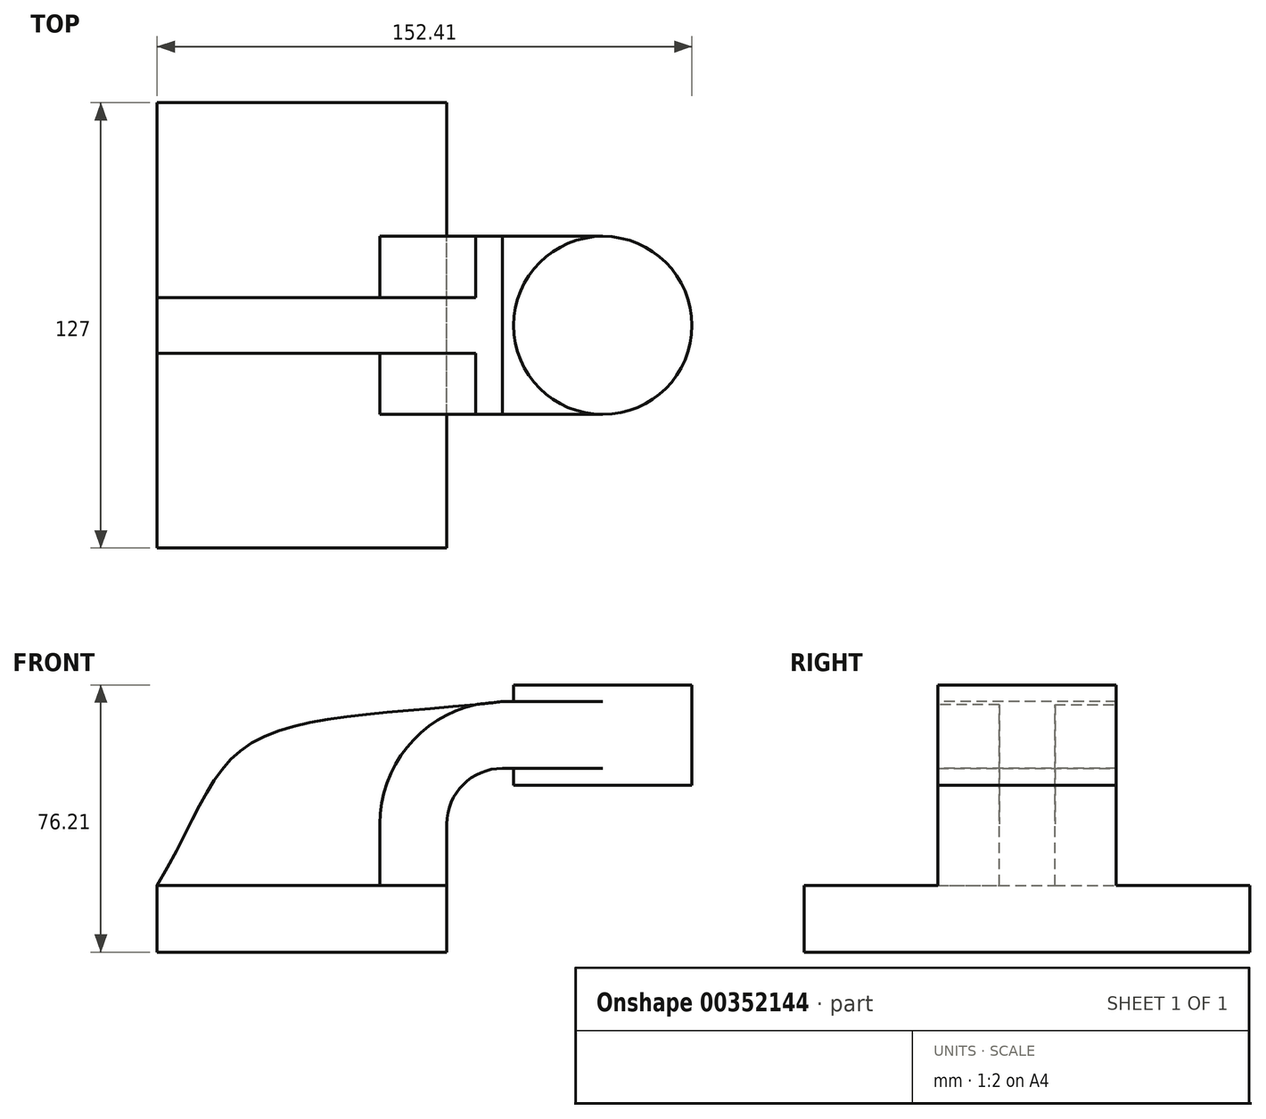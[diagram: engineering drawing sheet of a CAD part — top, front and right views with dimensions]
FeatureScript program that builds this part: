
annotation { "Feature Type Name" : "Feature", "Feature Type Description" : "" }
export const myFeature = defineFeature(function(context is Context, id is Id, definition is map)
    precondition{}
    {
        {
            var Q0;
            Q0=qCreatedBy(makeId("Front.planeOp"),FACE);
            var sketch = newSketch(context, id + "F0", { "sketchPlane" : qUnion([Q0])});
            skLineSegment(sketch, "E0.bottom", {"start": v(-41.27, -9.53) * mm, "end": v(41.28, -9.53) * mm});
            skLineSegment(sketch, "E0.top", {"start": v(-41.28, 9.53) * mm, "end": v(41.28, 9.53) * mm});
            skLineSegment(sketch, "E0.left", {"start": v(-41.28, -9.53) * mm, "end": v(-41.28, 9.53) * mm});
            skLineSegment(sketch, "E0.right", {"start": v(41.28, -9.53) * mm, "end": v(41.28, 9.52) * mm});
            skPoint(sketch, "E0.middle", {"position": v(0, 0) * mm});
            skLineSegment(sketch, "E1.bottom", {"start": v(111.13, 38.1) * mm, "end": v(60.33, 38.1) * mm});
            skLineSegment(sketch, "E1.top", {"start": v(111.12, 66.67) * mm, "end": v(60.33, 66.67) * mm});
            skLineSegment(sketch, "E1.left", {"start": v(111.13, 38.1) * mm, "end": v(111.13, 66.67) * mm});
            skLineSegment(sketch, "E1.right", {"start": v(60.33, 38.1) * mm, "end": v(60.33, 66.67) * mm});
            skPoint(sketch, "E1.middle", {"position": v(85.72, 52.39) * mm});
            skLineSegment(sketch, "E2", {"start": v(41.28, 9.52) * mm, "end": v(41.28, 27) * mm});
            skArc(sketch, "E3", {"start": v(57.15, 42.88) * mm, "mid": v(45.92, 38.23) * mm, "end": v(41.27, 27) * mm});
            skLineSegment(sketch, "E4", {"start": v(57.15, 42.88) * mm, "end": v(85.73, 42.88) * mm});
            skLineSegment(sketch, "E5.0", {"start": v(57.15, 61.93) * mm, "end": v(85.72, 61.93) * mm});
            skArc(sketch, "E5.1", {"start": v(57.15, 61.93) * mm, "mid": v(32.45, 51.7) * mm, "end": v(22.22, 27) * mm});
            skLineSegment(sketch, "E5.2", {"start": v(22.22, 9.52) * mm, "end": v(22.22, 27) * mm});
            skFitSpline(sketch, "E6", {"points": [v(-41.28, 9.52) * mm, v(-15.07, 49.64) * mm, v(57.15, 61.93) * mm], "startDerivative": vector(75.56, 125.27) * mm, "endDerivative": vector(161.69, 19.42) * mm});
            skLineSegment(sketch, "E7", {"start": v(85.72, 66.67) * mm, "end": v(85.72, 38.1) * mm});
            skSolve(sketch);
        }
        {
            var Q0;
            Q0=makeQuery(id+"F0.imprint","IMPRINT",FACE,{"disambiguationData":[TD([[makeQuery(id+"F0.imprint","IMPRINT",EDGE,{"derivedFrom":sQuery(id+"F0.wireOp",EDGE,"E0.bottom")}),1.0]])]});
            extrude(context, id + "F1", {"entities" : qUnion([Q0]), "endBound" : BoundingType.SYMMETRIC, "depth" : 127 * mm});
        }
        {
            var Q0;
            {var subQ0=sQuery(id+"F0.wireOp",EDGE,"E2");Q0=makeQuery(id+"F0.imprint","IMPRINT",FACE,{"disambiguationData":[TD([[makeQuery(id+"F0.imprint","IMPRINT",EDGE,{"derivedFrom":subQ0}),1.0]])]});}
            var Q1;
            {var subQ5=sQuery(id+"F0.wireOp",EDGE,"j8fLPQHC-WPwm-iJhR-GlT9-Asvy3SUJxMD6");Q1=makeQuery(id+"F0.imprint","IMPRINT",FACE,{"disambiguationData":[TD([[makeQuery(id+"F0.imprint","IMPRINT",EDGE,{"derivedFrom":subQ5}),-1.0]])]});}
            extrude(context, id + "F2", {"entities" : qUnion([Q0, Q1]), "operationType" : NewBodyOperationType.ADD, "endBound" : BoundingType.SYMMETRIC, "depth" : 50.8 * mm});
        }
        {
            var Q0;
            {var subQ3=sQuery(id+"F0.wireOp",EDGE,"E5.2");Q0=makeQuery(id+"F0.imprint","IMPRINT",FACE,{"disambiguationData":[TD([[makeQuery(id+"F0.imprint","IMPRINT",EDGE,{"derivedFrom":subQ3}),1.0]])]});}
            extrude(context, id + "F3", {"entities" : qUnion([Q0]), "operationType" : NewBodyOperationType.ADD, "endBound" : BoundingType.SYMMETRIC, "depth" : 15.88 * mm});
        }
        {
            var Q0;
            {var subQ0=sQuery(id+"F0.wireOp",EDGE,"E4");var subQ1=sQuery(id+"F0.wireOp",EDGE,"E1.right");var subQ2=makeQuery(id+"F0.imprint","INTERSECT",VERTEX,{"derivedFrom":[subQ1,subQ0]});Q0=makeQuery(id+"F0.imprint","IMPRINT",FACE,{"disambiguationData":[TD([[makeQuery(id+"F0.imprint","IMPRINT",EDGE,{"disambiguationData":[TD([[subQ2,-1.0]])],"derivedFrom":subQ1}),-1.0]])]});}
            extrude(context, id + "F4", {"entities" : qUnion([Q0]), "operationType" : NewBodyOperationType.ADD, "endBound" : BoundingType.SYMMETRIC, "depth" : 50.8 * mm});
        }
        {
            var Q0;
            {var subQ4=sQuery(id+"F0.wireOp",EDGE,"E1.left");Q0=makeQuery(id+"F0.imprint","IMPRINT",FACE,{"disambiguationData":[TD([[makeQuery(id+"F0.imprint","IMPRINT",EDGE,{"derivedFrom":subQ4}),1.0]])]});}
            var Q1;
            Q1=sQuery(id+"F0.wireOp",EDGE,"E7");
            revolve(context, id + "F5", {"operationType" : NewBodyOperationType.ADD, "entities" : qUnion([Q0]), "axis" : qUnion([Q1]), "revolveType" : RevolveType.FULL});
        }
    });
